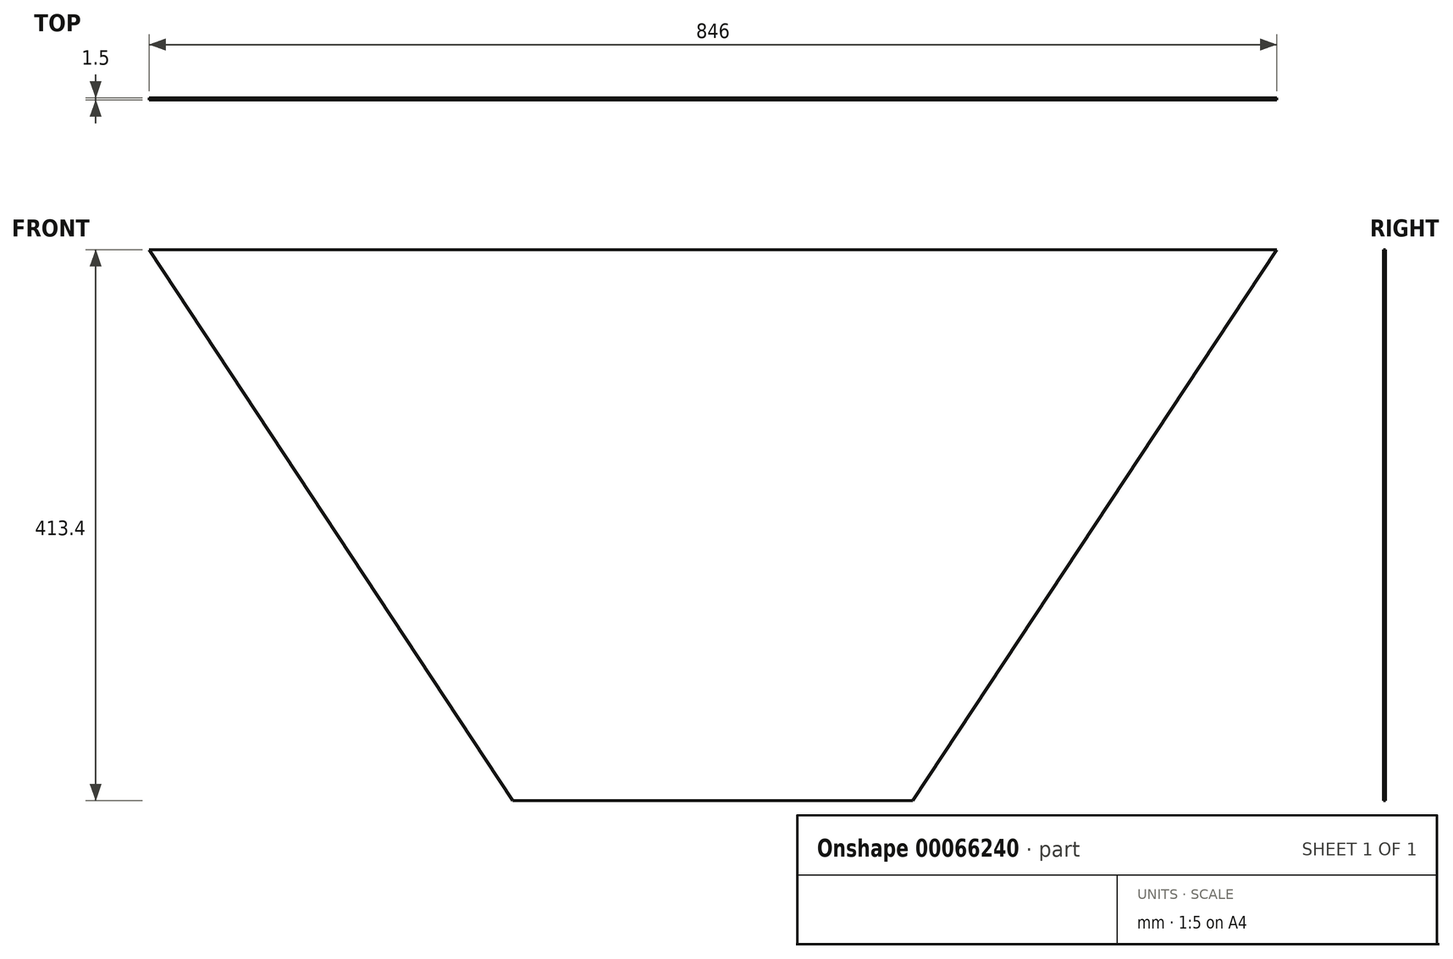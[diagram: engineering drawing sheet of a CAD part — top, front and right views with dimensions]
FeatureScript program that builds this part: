
annotation { "Feature Type Name" : "Feature", "Feature Type Description" : "" }
export const myFeature = defineFeature(function(context is Context, id is Id, definition is map)
    precondition{}
    {
        {
            var Q0;
            Q0=qCreatedBy(makeId("Front.planeOp"),FACE);
            var sketch = newSketch(context, id + "F0", { "sketchPlane" : qUnion([Q0])});
            skLineSegment(sketch, "E0", {"start": v(-516.14, 191.66) * mm, "end": v(329.86, 191.66) * mm});
            skLineSegment(sketch, "E1", {"start": v(329.86, 191.66) * mm, "end": v(56.86, -221.74) * mm});
            skLineSegment(sketch, "E2", {"start": v(56.86, -221.74) * mm, "end": v(-243.14, -221.74) * mm});
            skLineSegment(sketch, "E3", {"start": v(-243.14, -221.74) * mm, "end": v(-516.14, 191.66) * mm});
            skSolve(sketch);
        }
        {
            var Q0;
            Q0=makeQuery(id+"F0.imprint","IMPRINT",FACE,{"disambiguationData":[TD([[makeQuery(id+"F0.imprint","IMPRINT",EDGE,{"derivedFrom":sQuery(id+"F0.wireOp",EDGE,"E0")}),-1.0]])]});
            extrude(context, id + "F1", {"entities" : qUnion([Q0]), "depth" : 1.5 * mm});
        }
    });
